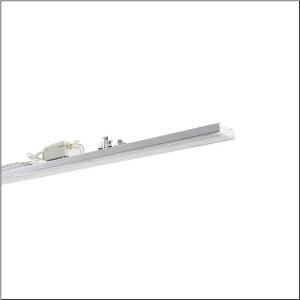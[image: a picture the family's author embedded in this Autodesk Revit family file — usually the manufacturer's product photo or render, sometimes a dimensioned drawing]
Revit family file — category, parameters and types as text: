
# Revit family: licross_11_recessed_ho_51te12dn4exm3s
name_source: partatom
category: Lighting Fixtures
units: mm (PartAtom-declared; Revit-internal decimal feet)

## family parameters
Cut with Voids When Loaded = No
Host = Face
Light Source = No
Part Type = Normal
Room Calculation Point = No
Round Connector Dimension = Use Diameter
Shared = No

## types (1)
- --- (1 x LED, 1000 lm, 7.2 W, 4000K)
    Apparent Load = 7 VA
    CIE Flux Codes = 66 91 98 100 100
    Color Rendering = 80
    Color Temperature = 4000K
    Default Elevation = 1800 mm
    Description = Licross 11 Recessed HO, luminaire insert, of sheet steel, galvanised, coil coated, white, length: 1.500mm, width: 66mm, height: 67mm, LED rated luminous flux: 14.030lm, light colour: 840, SDCM (Standard Deviation of Colour Matching)MacAdam ≤ 2 SDCM (initial), control gear: DALI 2 (for two DALI lines), with plug, 6-pole, with phase selection, for trunking rail, 14-core, mains connection: 220..240V, AC, 50/60Hz, rated input power: 81W, for trunking rail, 14-core, internal wiring halogen-free, for emergency light function, converter,control gear: single battery element, battery: LiFePO4, 9Ah, primary optical cover: cover, of PMMA, light emission: direct distribution, primary light characteristic: symmetric, protection rating (complete): IP54, insulation class (complete): insulation class I (protective earthing), certification: CE, UKCA, protection symbol: D if used in an environment with non-conductive dust loads with corresponding accessories, impact resistance: IK06, permissible ambient temperature for indoor applications: +5..+30°C, standard: EN 60598-2-22, LABS conformity tested according to VDMA 24364:2018-05, reducing of maximum allowable ambient temperature of 5°C with ceiling mounting, corresponds to IFS (International Featured Standards) requirements for safety and quality in the food industry, The light source and the operating device comply with the requirements of the Ecodesign Regulation (EU) 2019/2020 and are replaceable in accordance with this regulation, packaging unit: 1 piece
    Height = 58 mm
    Lamp = 1 x LED
    Lamp Light Flux = 1000 lm
    Lamp Power = 7.2 W
    Lamp count = 1
    Length = 1500 mm
    Luminous efficacy = 139 lm/W
    Manufacturer = Siteco
    ModVariant = No
    Model = 51TE12DN4EXM3S
    Mounting Place = Ceiling
    Mounting Type = Pendant
    Number of Poles = 1
    OnlyDefault = Yes
    Power Factor = 1
    Product Name = Licross 11 Recessed HO
    Product group = luminaire insert | ceiling pendant
    ProductGroupID = 901
    Protection Class = Protection class I
    Protection Degree = IP 54
    RLX_Detail_Level = 1
    RLX_Emergency_Light_Flux = 0 lm
    RLX_Emergency_Type = 0
    RLX_Emergency_Type_DB = No
    RlxData = <blob elided: 25241 chars, md5=9783b305>
    Socket = socket
    Standby Power = 0 W
    System Light Flux = 1000 lm
    System Power = 7 W
    Type Comments = : emergency light operation: 3 h
    Type Image = l_1296930.jpg
    URL = http://relux.com
    VarID = @adj_095483
    Voltage = 0 V
    Weight = 0.00 kg
    Width = 66 mm

## geometry (parser evidence)
native form markers: Blend x4, Sweep x12
no freeform markers — native parametric forms only
